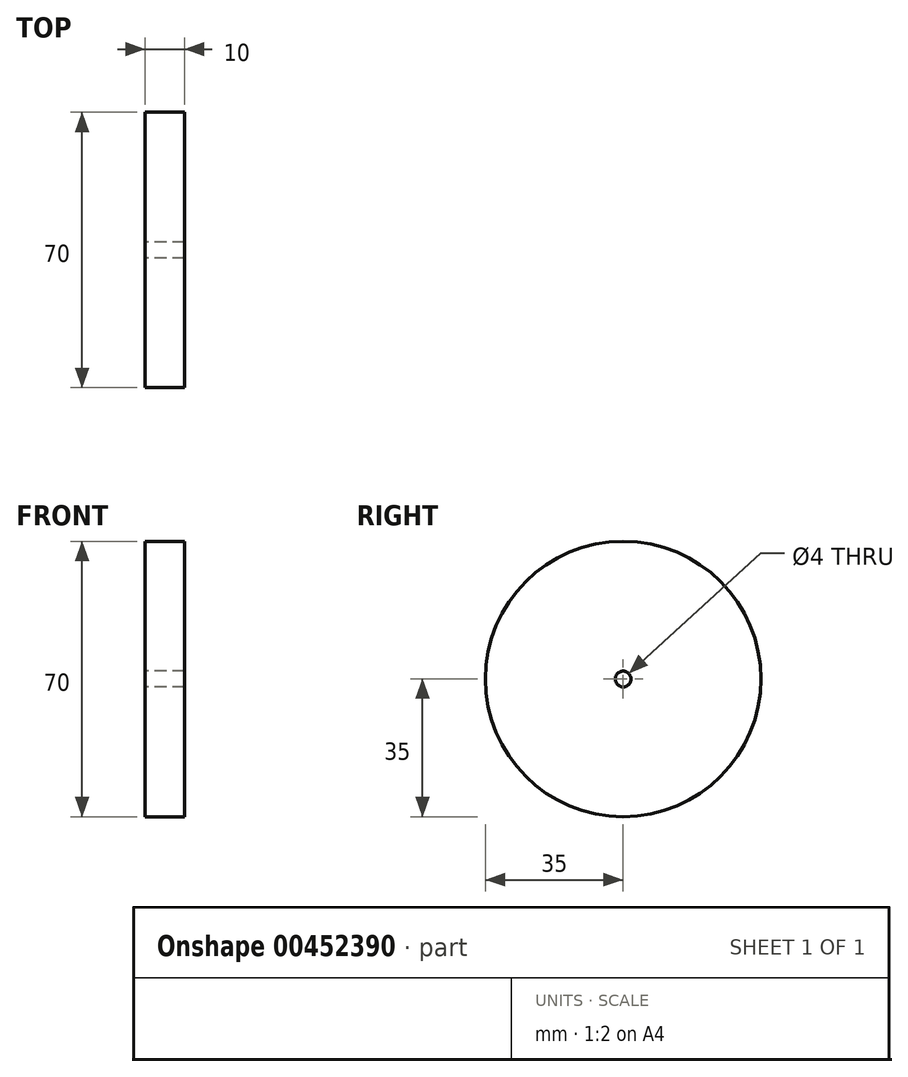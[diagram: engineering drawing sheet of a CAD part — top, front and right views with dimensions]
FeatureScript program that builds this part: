
annotation { "Feature Type Name" : "Feature", "Feature Type Description" : "" }
export const myFeature = defineFeature(function(context is Context, id is Id, definition is map)
    precondition{}
    {
        {
            var Q0;
            Q0=qCreatedBy(makeId("Right.planeOp"),FACE);
            var sketch = newSketch(context, id + "F0", { "sketchPlane" : qUnion([Q0])});
            skCircle(sketch, "E0", {"center": v(0, 0) * mm, "radius": 35 * mm});
            skCircle(sketch, "E1", {"center": v(0, 0) * mm, "radius": 2 * mm});
            skSolve(sketch);
        }
        {
            var Q0;
            Q0 = qSketchRegion(id + "F0", true);
            extrude(context, id + "F1", {"entities" : qUnion([Q0]), "depth" : 5 * mm, "hasSecondDirection" : true, "secondDirectionOppositeDirection" : true, "secondDirectionDepth" : 5 * mm});
        }
    });
